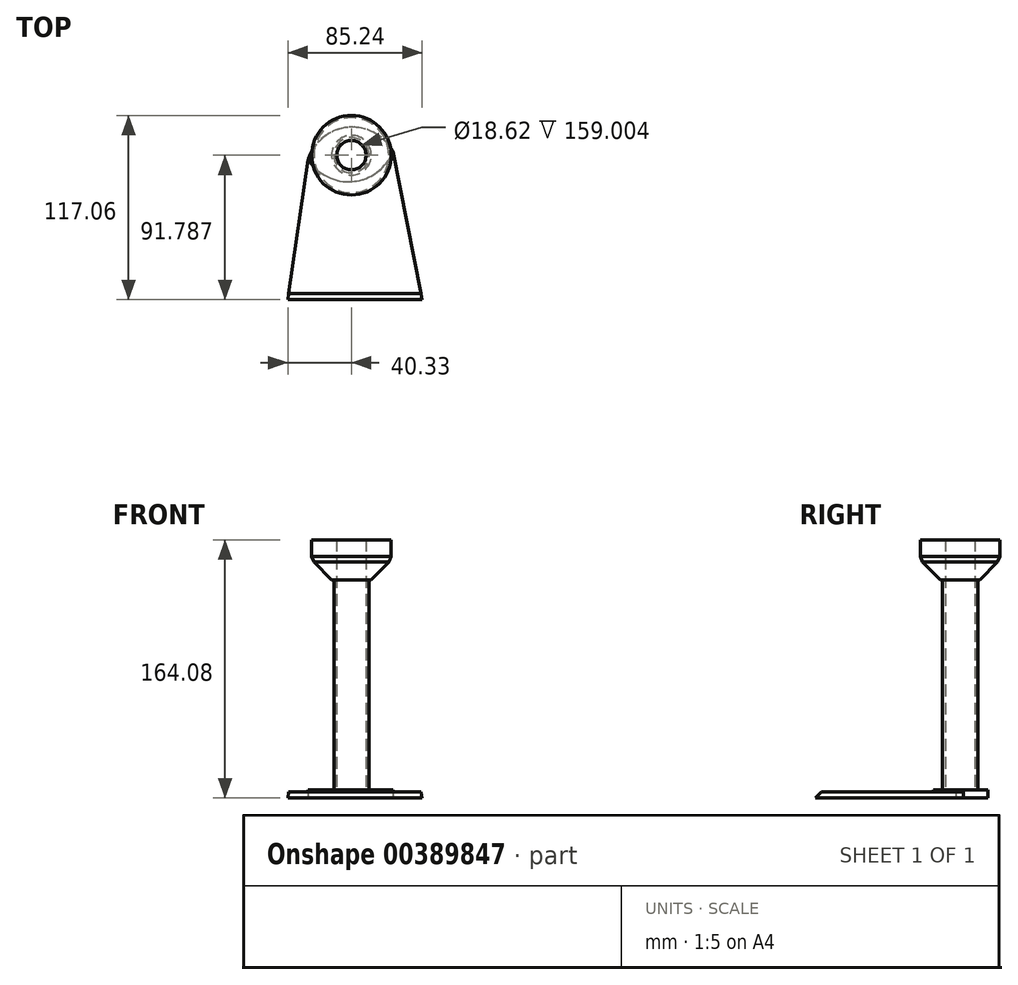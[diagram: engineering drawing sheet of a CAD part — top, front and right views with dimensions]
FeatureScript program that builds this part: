
annotation { "Feature Type Name" : "Feature", "Feature Type Description" : "" }
export const myFeature = defineFeature(function(context is Context, id is Id, definition is map)
    precondition{}
    {
        {
            var Q0;
            Q0=qCreatedBy(makeId("Top.planeOp"),FACE);
            var sketch = newSketch(context, id + "F0", { "sketchPlane" : qUnion([Q0])});
            skArc(sketch, "E0", {"start": v(26.4, 43.04) * mm, "mid": v(-2.17, 58.48) * mm, "end": v(-27.46, 38.12) * mm});
            skLineSegment(sketch, "E1", {"start": v(26.4, 43.04) * mm, "end": v(45.16, -52.24) * mm});
            skLineSegment(sketch, "E2", {"start": v(45.16, -52.24) * mm, "end": v(-40.52, -52.24) * mm});
            skLineSegment(sketch, "E3", {"start": v(-40.52, -52.24) * mm, "end": v(-27.46, 38.12) * mm});
            skSolve(sketch);
        }
        {
            var Q0;
            Q0=makeQuery(id+"F0.imprint","IMPRINT",FACE,{"disambiguationData":[TD([[makeQuery(id+"F0.imprint","IMPRINT",EDGE,{"derivedFrom":sQuery(id+"F0.wireOp",EDGE,"E0")}),1.0]])]});
            extrude(context, id + "F1", {"entities" : qUnion([Q0]), "depth" : 3.8 * mm});
        }
        {
            var Q0;
            Q0=makeQuery(id+"F1.opExtrude","CAP_FACE",FACE,{"disambiguationData":[OSD([sQuery(id+"F0.wireOp",EDGE,"E0"),sQuery(id+"F0.wireOp",EDGE,"E1"),sQuery(id+"F0.wireOp",EDGE,"E2"),sQuery(id+"F0.wireOp",EDGE,"E3")])],"isStart":false});
            var sketch = newSketch(context, id + "F2", { "sketchPlane" : qUnion([Q0])});
            skArc(sketch, "E4", {"start": v(-27.46, 38.12) * mm, "mid": v(0.98, 24.1) * mm, "end": v(26.4, 43.04) * mm});
            skSolve(sketch);
        }
        {
            var Q0;
            Q0=makeQuery(id+"F1.opExtrude","CAP_EDGE",EDGE,{"disambiguationData":[OSD([sQuery(id+"F0.wireOp",EDGE,"E2")])],"isStart":false});
            chamfer(context, id + "F3", {"entities" : qUnion([Q0]), "width" : 5.08 * mm, "tangentPropagation" : true});
        }
        {
            var Q0;
            Q0=makeQuery(id+"F2.imprint","IMPRINT",FACE,{"disambiguationData":[TD([[makeQuery(id+"F2.imprint","IMPRINT",EDGE,{"derivedFrom":sQuery(id+"F2.wireOp",EDGE,"E4")}),1.0]])]});
            extrude(context, id + "F4", {"entities" : qUnion([Q0]), "operationType" : NewBodyOperationType.ADD, "depth" : 1.27 * mm});
        }
        {
            var Q0;
            Q0=makeQuery(id+"F4.opExtrude","CAP_FACE",FACE,{"disambiguationData":[OSD([sQuery(id+"F0.wireOp",EDGE,"E0"),sQuery(id+"F2.wireOp",EDGE,"E4")])],"isStart":false});
            var sketch = newSketch(context, id + "F5", { "sketchPlane" : qUnion([Q0])});
            skCircle(sketch, "E5", {"center": v(0, 40.82) * mm, "radius": 11.19 * mm});
            skCircle(sketch, "E6", {"center": v(0, 40.82) * mm, "radius": 9.31 * mm});
            skSolve(sketch);
        }
        {
            var Q0;
            Q0=makeQuery(id+"F5.imprint","IMPRINT",FACE,{"disambiguationData":[TD([[makeQuery(id+"F5.imprint","IMPRINT",EDGE,{"derivedFrom":sQuery(id+"F5.wireOp",EDGE,"E5")}),1.0]])]});
            extrude(context, id + "F6", {"entities" : qUnion([Q0]), "operationType" : NewBodyOperationType.ADD, "depth" : 133.6 * mm});
        }
        {
            var Q0;
            Q0=makeQuery(id+"F6.opExtrude","CAP_FACE",FACE,{"disambiguationData":[OSD([sQuery(id+"F5.wireOp",EDGE,"E5"),sQuery(id+"F5.wireOp",EDGE,"E6")])],"isStart":false});
            var sketch = newSketch(context, id + "F7", { "sketchPlane" : qUnion([Q0])});
            skCircle(sketch, "E7", {"center": v(0, 40.82) * mm, "radius": 25.28 * mm});
            skSolve(sketch);
        }
        {
            var Q0;
            Q0=makeQuery(id+"F7.imprint","IMPRINT",FACE,{"disambiguationData":[TD([[makeQuery(id+"F7.imprint","IMPRINT",EDGE,{"derivedFrom":sQuery(id+"F7.wireOp",EDGE,"E7")}),1.0]])]});
            var Q1;
            Q1=makeQuery(id+"F7.imprint","IMPRINT",FACE,{"disambiguationData":[TD([[makeQuery(id+"F7.imprint","IMPRINT",EDGE,{"derivedFrom":makeQuery(id+"F6.opExtrude","CAP_EDGE",EDGE,{"disambiguationData":[OSD([sQuery(id+"F5.wireOp",EDGE,"E5")])],"isStart":false})}),1.0]])]});
            extrude(context, id + "F8", {"entities" : qUnion([Q0, Q1]), "operationType" : NewBodyOperationType.ADD, "depth" : 25.4 * mm});
        }
        {
            var Q0;
            Q0=makeQuery(id+"F8.opExtrude","CAP_EDGE",EDGE,{"disambiguationData":[OSD([sQuery(id+"F7.wireOp",EDGE,"E7")])],"isStart":true});
            chamfer(context, id + "F9", {"entities" : qUnion([Q0]), "width" : 12.7 * mm, "tangentPropagation" : true});
        }
        {
            var Q0;
            {var subQ0=sQuery(id+"F7.wireOp",EDGE,"E7");Q0=makeQuery(id+"F9.opChamfer","BLEND_EDGE",EDGE,{"blendedFrom":[makeQuery(id+"F8.opExtrude","CAP_EDGE",EDGE,{"disambiguationData":[OSD([subQ0])],"isStart":true}),makeQuery(id+"F8.opExtrude","SWEPT_FACE",FACE,{"disambiguationData":[OSD([subQ0])]})],"blendedInto":[makeQuery(id+"F8.opExtrude","SWEPT_FACE",FACE,{"disambiguationData":[OSD([subQ0])]})]});}
            chamfer(context, id + "F10", {"entities" : qUnion([Q0]), "width" : 5.08 * mm, "tangentPropagation" : true});
        }
    });
